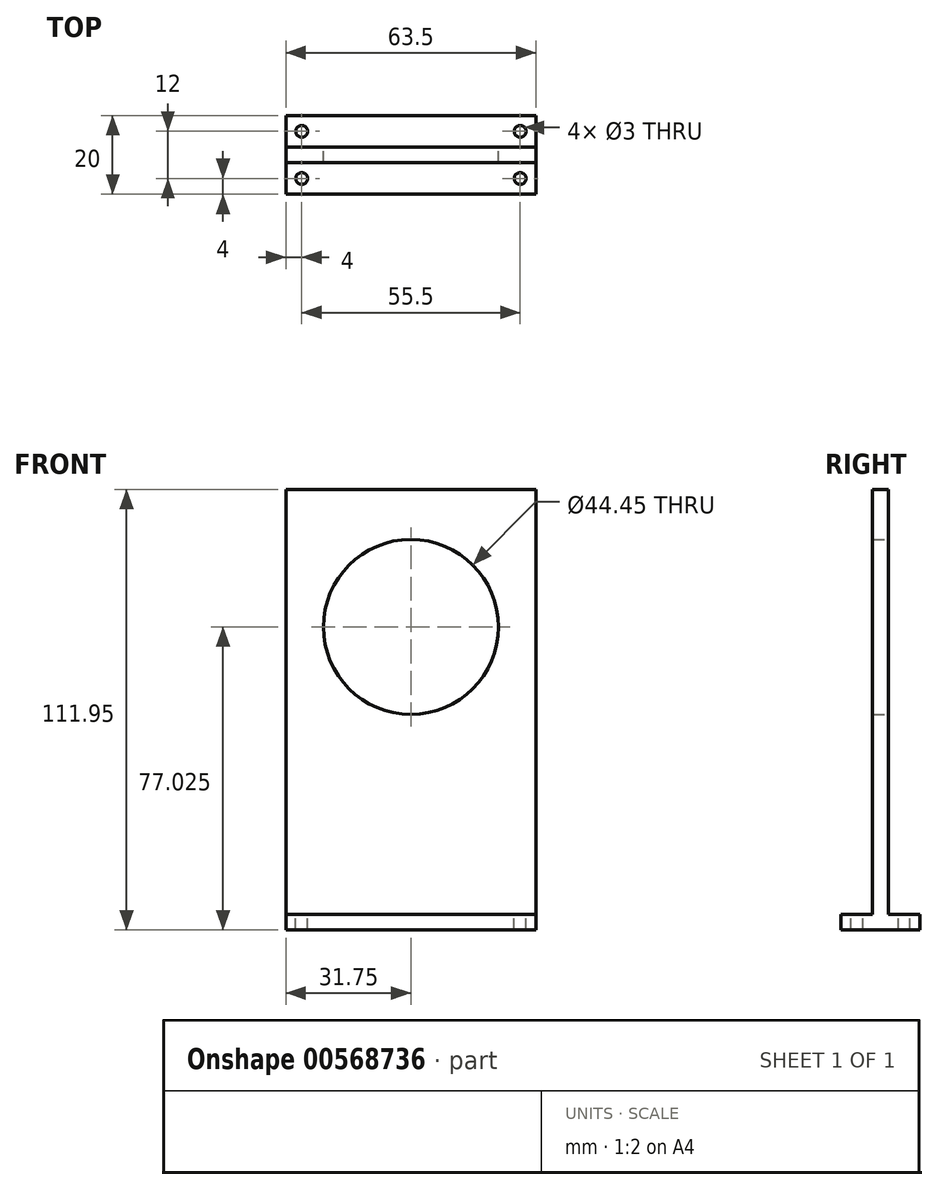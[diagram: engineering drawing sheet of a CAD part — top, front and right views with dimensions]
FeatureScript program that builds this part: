
annotation { "Feature Type Name" : "Feature", "Feature Type Description" : "" }
export const myFeature = defineFeature(function(context is Context, id is Id, definition is map)
    precondition{}
    {
        {
            var Q0;
            Q0=qCreatedBy(makeId("Front.planeOp"),FACE);
            var sketch = newSketch(context, id + "F0", { "sketchPlane" : qUnion([Q0])});
            skLineSegment(sketch, "E0.bottom", {"start": v(0, 0) * mm, "end": v(63.5, 0) * mm});
            skLineSegment(sketch, "E0.top", {"start": v(0, 107.95) * mm, "end": v(63.5, 107.95) * mm});
            skLineSegment(sketch, "E0.left", {"start": v(0, 0) * mm, "end": v(0, 107.95) * mm});
            skLineSegment(sketch, "E0.right", {"start": v(63.5, 0) * mm, "end": v(63.5, 107.95) * mm});
            skCircle(sketch, "E1", {"center": v(31.75, 73.02) * mm, "radius": 22.23 * mm});
            skSolve(sketch);
        }
        {
            var Q0;
            Q0=makeQuery(id+"F0.imprint","IMPRINT",FACE,{"disambiguationData":[TD([[makeQuery(id+"F0.imprint","IMPRINT",EDGE,{"derivedFrom":sQuery(id+"F0.wireOp",EDGE,"E0.bottom")}),1.0]])]});
            extrude(context, id + "F1", {"entities" : qUnion([Q0]), "endBound" : BoundingType.SYMMETRIC, "depth" : 4 * mm, "offsetDistance" : 25.4 * mm});
        }
        {
            var Q0;
            Q0=qCreatedBy(makeId("Front.planeOp"),FACE);
            var sketch = newSketch(context, id + "F2", { "sketchPlane" : qUnion([Q0])});
            skLineSegment(sketch, "E2", {"start": v(63.5, 0) * mm, "end": v(0, 0) * mm});
            skLineSegment(sketch, "E3", {"start": v(0, 0) * mm, "end": v(0, -4) * mm});
            skLineSegment(sketch, "E4", {"start": v(0, -4) * mm, "end": v(63.5, -4) * mm});
            skLineSegment(sketch, "E5", {"start": v(63.5, -4) * mm, "end": v(63.5, 0) * mm});
            skSolve(sketch);
        }
        {
            var Q0;
            Q0 = qSketchRegion(id + "F2", true);
            extrude(context, id + "F3", {"entities" : qUnion([Q0]), "operationType" : NewBodyOperationType.ADD, "endBound" : BoundingType.SYMMETRIC, "depth" : 20 * mm, "offsetDistance" : 25.4 * mm});
        }
        {
            var Q0;
            {var subQ1=sQuery(id+"F2.wireOp",EDGE,"E5");var subQ2=sQuery(id+"F2.wireOp",EDGE,"E3");var subQ3=sQuery(id+"F2.wireOp",EDGE,"E2");Q0=makeQuery(id+"F3.boolean.opBoolean","SPLIT",FACE,{"disambiguationData":[TD([makeQuery(id+"F3.opExtrude","CAP_FACE",FACE,{"disambiguationData":[OSD([subQ3,subQ2,sQuery(id+"F2.wireOp",EDGE,"E4"),subQ1])],"isStart":true})])],"derivedFrom":makeQuery(id+"F3.opExtrude","SWEPT_FACE",FACE,{"disambiguationData":[OSD([subQ3])]})});}
            var sketch = newSketch(context, id + "F4", { "sketchPlane" : qUnion([Q0])});
            skCircle(sketch, "E6", {"center": v(4, 6) * mm, "radius": 1.5 * mm});
            skCircle(sketch, "E7", {"center": v(59.5, 6) * mm, "radius": 1.5 * mm});
            skSolve(sketch);
        }
        {
            var Q0;
            Q0 = qSketchRegion(id + "F4", true);
            extrude(context, id + "F5", {"entities" : qUnion([Q0]), "operationType" : NewBodyOperationType.REMOVE, "oppositeDirection" : true, "depth" : 25 * mm, "offsetDistance" : 25 * mm});
        }
        {
            var Q0;
            {var subQ0=sQuery(id+"F2.wireOp",EDGE,"E5");var subQ1=sQuery(id+"F2.wireOp",EDGE,"E3");var subQ2=sQuery(id+"F2.wireOp",EDGE,"E2");Q0=makeQuery(id+"F3.boolean.opBoolean","SPLIT",FACE,{"disambiguationData":[TD([makeQuery(id+"F3.opExtrude","CAP_FACE",FACE,{"disambiguationData":[OSD([subQ2,subQ1,sQuery(id+"F2.wireOp",EDGE,"E4"),subQ0])],"isStart":false})])],"derivedFrom":makeQuery(id+"F3.opExtrude","SWEPT_FACE",FACE,{"disambiguationData":[OSD([subQ2])]})});}
            var sketch = newSketch(context, id + "F6", { "sketchPlane" : qUnion([Q0])});
            skCircle(sketch, "E8", {"center": v(4, -6) * mm, "radius": 1.5 * mm});
            skCircle(sketch, "E9", {"center": v(59.5, -6) * mm, "radius": 1.5 * mm});
            skSolve(sketch);
        }
        {
            var Q0;
            Q0 = qSketchRegion(id + "F6", true);
            extrude(context, id + "F7", {"entities" : qUnion([Q0]), "operationType" : NewBodyOperationType.REMOVE, "oppositeDirection" : true, "depth" : 25 * mm, "offsetDistance" : 25 * mm});
        }
    });
